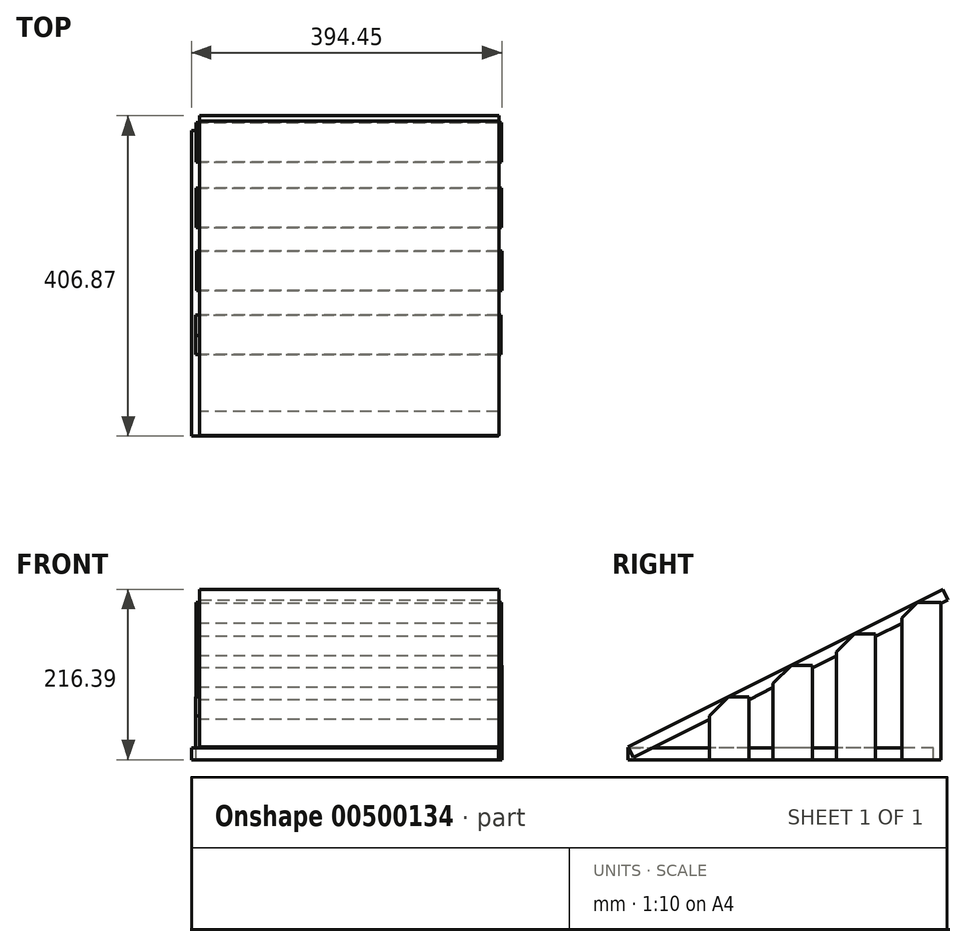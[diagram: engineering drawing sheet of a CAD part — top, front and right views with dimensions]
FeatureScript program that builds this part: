
annotation { "Feature Type Name" : "Feature", "Feature Type Description" : "" }
export const myFeature = defineFeature(function(context is Context, id is Id, definition is map)
    precondition{}
    {
        {
            var Q0;
            Q0=qCreatedBy(makeId("Top.planeOp"),FACE);
            var sketch = newSketch(context, id + "F0", { "sketchPlane" : qUnion([Q0])});
            skLineSegment(sketch, "E0.bottom", {"start": v(-200.51, 187.45) * mm, "end": v(189.49, 187.45) * mm});
            skLineSegment(sketch, "E0.top", {"start": v(-200.51, -200.55) * mm, "end": v(189.49, -200.55) * mm});
            skLineSegment(sketch, "E0.left", {"start": v(-200.51, 187.45) * mm, "end": v(-200.51, -200.55) * mm});
            skLineSegment(sketch, "E0.right", {"start": v(189.49, 187.45) * mm, "end": v(189.49, -200.55) * mm});
            skSolve(sketch);
        }
        {
            var Q0;
            Q0=makeQuery(id+"F0.imprint","IMPRINT",FACE,{"disambiguationData":[TD([[makeQuery(id+"F0.imprint","IMPRINT",EDGE,{"derivedFrom":sQuery(id+"F0.wireOp",EDGE,"E0.bottom")}),-1.0]])]});
            extrude(context, id + "F1", {"entities" : qUnion([Q0]), "depth" : 15 * mm});
        }
        {
            var Q0;
            Q0=qCreatedBy(makeId("Right.planeOp"),FACE);
            var sketch = newSketch(context, id + "F2", { "sketchPlane" : qUnion([Q0])});
            skLineSegment(sketch, "E1", {"start": v(-200.18, 16.45) * mm, "end": v(199.61, 216.39) * mm});
            skSolve(sketch);
        }
        {
            var Q0;
            Q0=sQuery(id+"F2.wireOp",EDGE,"E1");
            extrude(context, id + "F3", {"bodyType" : ToolBodyType.SURFACE, "surfaceEntities" : qUnion([Q0]), "depth" : 190 * mm});
        }
        {
            var Q0;
            Q0=makeQuery(id+"F3.opExtrude","SWEPT_BODY",BODY,{"disambiguationData":[OSD([sQuery(id+"F2.wireOp",EDGE,"E1")])]});
            var Q1;
            Q1=qCreatedBy(makeId("Right.planeOp"),FACE);
            mirror(context, id + "F4", {"entities" : qUnion([Q0]), "mirrorPlane" : qUnion([Q1])});
        }
        {
            var Q0;
            Q0=makeQuery(id+"F3.opExtrude","SWEPT_FACE",FACE,{"disambiguationData":[OSD([sQuery(id+"F2.wireOp",EDGE,"E1")])]});
            extrude(context, id + "F5", {"entities" : qUnion([Q0]), "operationType" : NewBodyOperationType.ADD, "depth" : 15 * mm});
        }
        {
            var Q0;
            Q0=makeQuery(id+"F4.opPattern","COPY",FACE,{"derivedFrom":makeQuery(id+"F3.opExtrude","SWEPT_FACE",FACE,{"disambiguationData":[OSD([sQuery(id+"F2.wireOp",EDGE,"E1")])]}),"instanceName":"1"});
            extrude(context, id + "F6", {"entities" : qUnion([Q0]), "operationType" : NewBodyOperationType.ADD, "depth" : 15 * mm});
        }
        {
            var Q0;
            Q0=qCreatedBy(makeId("Top.planeOp"),FACE);
            var sketch = newSketch(context, id + "F7", { "sketchPlane" : qUnion([Q0])});
            skLineSegment(sketch, "E2", {"start": v(-194.81, 197.4) * mm, "end": v(193.19, 197.4) * mm});
            skSolve(sketch);
        }
        {
            var Q0;
            Q0=sQuery(id+"F7.wireOp",EDGE,"E2");
            extrude(context, id + "F8", {"bodyType" : ToolBodyType.SURFACE, "surfaceEntities" : qUnion([Q0]), "depth" : 200 * mm});
        }
        {
            var Q0;
            Q0=makeQuery(id+"F8.opExtrude","SWEPT_FACE",FACE,{"disambiguationData":[OSD([sQuery(id+"F7.wireOp",EDGE,"E2")])]});
            extrude(context, id + "F9", {"entities" : qUnion([Q0]), "operationType" : NewBodyOperationType.ADD, "depth" : 50 * mm});
        }
        {
            var Q0;
            {var subQ0=sQuery(id+"F7.wireOp",EDGE,"E2");Q0=makeQuery(id+"F9.opExtrude","CAP_EDGE",EDGE,{"disambiguationData":[OSD([subQ0]),TDD([makeQuery(id+"F8.opExtrude","CAP_EDGE",EDGE,{"disambiguationData":[OSD([subQ0])],"isStart":false})])],"isStart":false});}
            chamfer(context, id + "F10", {"entities" : qUnion([Q0]), "width" : 20 * mm, "tangentPropagation" : true});
        }
        {
            var Q0;
            Q0=qCreatedBy(makeId("Top.planeOp"),FACE);
            var sketch = newSketch(context, id + "F11", { "sketchPlane" : qUnion([Q0])});
            skLineSegment(sketch, "E3", {"start": v(-194.75, 114.32) * mm, "end": v(193.25, 114.32) * mm});
            skSolve(sketch);
        }
        {
            var Q0;
            Q0=sQuery(id+"F11.wireOp",EDGE,"E3");
            extrude(context, id + "F12", {"bodyType" : ToolBodyType.SURFACE, "surfaceEntities" : qUnion([Q0]), "depth" : 160 * mm});
        }
        {
            var Q0;
            Q0=makeQuery(id+"F12.opExtrude","SWEPT_FACE",FACE,{"disambiguationData":[OSD([sQuery(id+"F11.wireOp",EDGE,"E3")])]});
            extrude(context, id + "F13", {"entities" : qUnion([Q0]), "operationType" : NewBodyOperationType.ADD, "depth" : 50 * mm});
        }
        {
            var Q0;
            {var subQ0=sQuery(id+"F11.wireOp",EDGE,"E3");Q0=makeQuery(id+"F13.opExtrude","CAP_EDGE",EDGE,{"disambiguationData":[OSD([subQ0]),TDD([makeQuery(id+"F12.opExtrude","CAP_EDGE",EDGE,{"disambiguationData":[OSD([subQ0])],"isStart":false})])],"isStart":false});}
            chamfer(context, id + "F14", {"entities" : qUnion([Q0]), "width" : 23 * mm, "tangentPropagation" : true});
        }
        {
            var Q0;
            Q0=qCreatedBy(makeId("Top.planeOp"),FACE);
            var sketch = newSketch(context, id + "F15", { "sketchPlane" : qUnion([Q0])});
            skLineSegment(sketch, "E4", {"start": v(-194.06, 34.14) * mm, "end": v(193.94, 34.14) * mm});
            skSolve(sketch);
        }
        {
            var Q0;
            Q0=sQuery(id+"F15.wireOp",EDGE,"E4");
            extrude(context, id + "F16", {"bodyType" : ToolBodyType.SURFACE, "surfaceEntities" : qUnion([Q0]), "depth" : 120 * mm});
        }
        {
            var Q0;
            Q0=makeQuery(id+"F16.opExtrude","SWEPT_FACE",FACE,{"disambiguationData":[OSD([sQuery(id+"F15.wireOp",EDGE,"E4")])]});
            extrude(context, id + "F17", {"entities" : qUnion([Q0]), "operationType" : NewBodyOperationType.ADD, "depth" : 50 * mm});
        }
        {
            var Q0;
            {var subQ0=sQuery(id+"F15.wireOp",EDGE,"E4");Q0=makeQuery(id+"F17.opExtrude","CAP_EDGE",EDGE,{"disambiguationData":[OSD([subQ0]),TDD([makeQuery(id+"F16.opExtrude","CAP_EDGE",EDGE,{"disambiguationData":[OSD([subQ0])],"isStart":false})])],"isStart":false});}
            chamfer(context, id + "F18", {"entities" : qUnion([Q0]), "width" : 23 * mm, "tangentPropagation" : true});
        }
        {
            var Q0;
            Q0=qCreatedBy(makeId("Top.planeOp"),FACE);
            var sketch = newSketch(context, id + "F19", { "sketchPlane" : qUnion([Q0])});
            skLineSegment(sketch, "E5", {"start": v(-195.45, -46.9) * mm, "end": v(192.55, -46.9) * mm});
            skSolve(sketch);
        }
        {
            var Q0;
            Q0=sQuery(id+"F19.wireOp",EDGE,"E5");
            extrude(context, id + "F20", {"bodyType" : ToolBodyType.SURFACE, "surfaceEntities" : qUnion([Q0]), "depth" : 80 * mm});
        }
        {
            var Q0;
            Q0=makeQuery(id+"F20.opExtrude","SWEPT_FACE",FACE,{"disambiguationData":[OSD([sQuery(id+"F19.wireOp",EDGE,"E5")])]});
            extrude(context, id + "F21", {"entities" : qUnion([Q0]), "operationType" : NewBodyOperationType.ADD, "depth" : 50 * mm});
        }
        {
            var Q0;
            {var subQ0=sQuery(id+"F19.wireOp",EDGE,"E5");Q0=makeQuery(id+"F21.opExtrude","CAP_EDGE",EDGE,{"disambiguationData":[OSD([subQ0]),TDD([makeQuery(id+"F20.opExtrude","CAP_EDGE",EDGE,{"disambiguationData":[OSD([subQ0])],"isStart":false})])],"isStart":false});}
            chamfer(context, id + "F22", {"entities" : qUnion([Q0]), "width" : 24 * mm, "tangentPropagation" : true});
        }
    });
